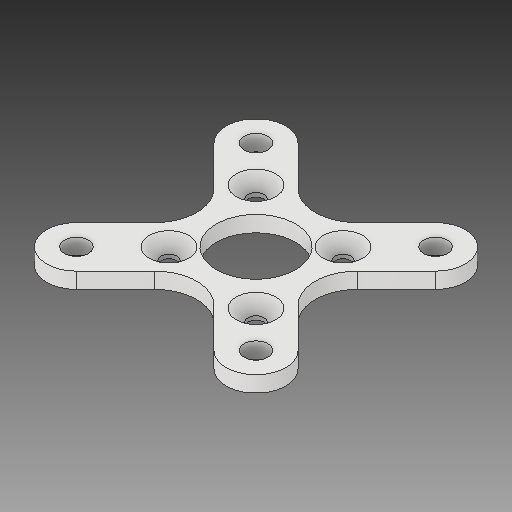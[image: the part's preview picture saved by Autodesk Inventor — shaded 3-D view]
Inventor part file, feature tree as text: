
AUTODESK INVENTOR PART (.ipt)
format: ipt  version: 2019 (Build 230136000, 136)  size: 148,992 bytes
history: imported  units: mm
features: imported_body x1
ambient origin geometry x8: Origin, YZ Plane, XZ Plane, XY Plane, X Axis, Y Axis, Z Axis, Center Point
bodies: Solide1 (imported_parasolid), Body1 (imported_parasolid)
feature tree (1):
  imported_body  NMx_Import_Brep_tag  [imported B-rep: ~31 faces, bbox_mm=[27.930718, 2.0, 27.930718]]
